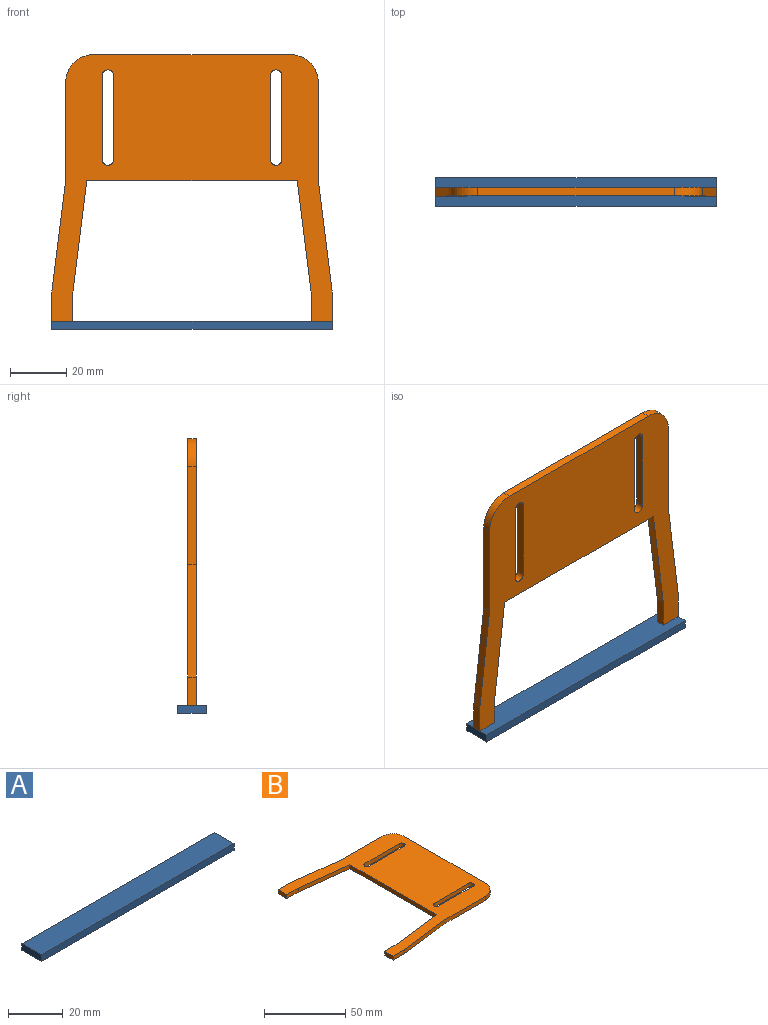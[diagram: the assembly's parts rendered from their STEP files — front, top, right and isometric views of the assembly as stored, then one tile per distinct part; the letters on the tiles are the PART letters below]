
ASSEMBLY  parts=2 mates=1
PART A: 6 faces, bbox 100x10x3 mm
  f0: plane 10x3mm, normal (-1,0,0), area 30mm2, adj f1,f3,f4,f5
  f1: plane 100x3mm, normal (0,-1,0), area 300mm2, adj f0,f2,f4,f5
  f2: plane 10x3mm, normal (1,0,0), area 30mm2, adj f1,f3,f4,f5
  f3: plane 100x3mm, normal (0,1,0), area 300mm2, adj f0,f2,f4,f5
  f4: plane 100x10mm, normal (0,0,1), area 1000mm2, adj f0,f1,f2,f3
  f5: plane 100x10mm, normal (0,0,-1), area 1000mm2, adj f0,f1,f2,f3
PART B: 26 faces, bbox 95x100x3 mm
  f0: cylinder r=2mm len=4mm, axis (0,0,-1), area 18.8mm2, adj f1,f23,f24,f25
  f1: plane 30x3mm, normal (0,-1,0), area 90mm2, adj f0,f2,f24,f25
  f2: cylinder r=2mm len=4mm, axis (0,0,-1), area 18.8mm2, adj f1,f23,f24,f25
  f3: plane 10x3mm, normal (0,-1,0), area 30mm2, adj f4,f21,f24,f25
  f4: plane 40x5mm, normal (0.12,-0.99,0), area 120.9mm2, adj f3,f5,f24,f25
  f5: plane 35x3mm, normal (0,-1,0), area 105mm2, adj f4,f6,f24,f25
  f6: cylinder r=10mm len=10mm, axis (0,0,-1), area 47.1mm2, adj f5,f7,f24,f25
  f7: plane 70x3mm, normal (1,0,0), area 210mm2, adj f6,f8,f24,f25
  f8: cylinder r=10mm len=10mm, axis (0,0,-1), area 47.1mm2, adj f7,f9,f24,f25
  f9: plane 35x3mm, normal (0,1,0), area 105mm2, adj f8,f10,f24,f25
  f10: plane 40x5mm, normal (0.12,0.99,0), area 120.9mm2, adj f9,f11,f24,f25
  f11: plane 10x3mm, normal (0,1,0), area 30mm2, adj f10,f12,f24,f25
  f12: plane 7.5x3mm, normal (-1,0,0), area 22.5mm2, adj f11,f13,f24,f25
  f13: plane 10x3mm, normal (0,-1,0), area 30mm2, adj f12,f14,f24,f25
  f14: plane 40x5mm, normal (-0.12,-0.99,0), area 120.9mm2, adj f13,f15,f24,f25
  f15: plane 75x3mm, normal (-1,0,0), area 225mm2, adj f14,f16,f24,f25
  f16: plane 40x5mm, normal (-0.12,0.99,0), area 120.9mm2, adj f15,f17,f24,f25
  f17: plane 10x3mm, normal (0,1,0), area 30mm2, adj f16,f21,f24,f25
  f18: plane 30x3mm, normal (0,1,0), area 90mm2, adj f19,f22,f24,f25
  f19: cylinder r=2mm len=4mm, axis (0,0,-1), area 18.8mm2, adj f18,f20,f24,f25
  f20: plane 30x3mm, normal (0,-1,0), area 90mm2, adj f19,f22,f24,f25
  f21: plane 7.5x3mm, normal (-1,0,0), area 22.5mm2, adj f3,f17,f24,f25
  f22: cylinder r=2mm len=4mm, axis (0,0,-1), area 18.8mm2, adj f18,f20,f24,f25
  f23: plane 30x3mm, normal (0,1,0), area 90mm2, adj f0,f2,f24,f25
  f24: plane 100x95mm, normal (0,0,1), area 4491.9mm2, adj f0,f1,f2,f3,f4,f5,f6,f7
  f25: plane 100x95mm, normal (0,0,-1), area 4491.9mm2, adj f0,f1,f2,f3,f4,f5,f6,f7
PLACE A t=(4.53,-1.92,-79.57)mm
PLACE B rot(axis=(0.58,-0.58,0.58),120deg) t=(21.14,-4.26,-35.89)mm
MATE fastened A.f4 <-> B.f21  axis (0,0,1) through (69.93,-5.76,-76.57)mm
